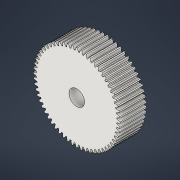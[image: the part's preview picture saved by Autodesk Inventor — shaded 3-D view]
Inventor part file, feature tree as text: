
AUTODESK INVENTOR PART (.ipt)
format: ipt  version: 2021 (Build 250183000, 183)  size: 414,720 bytes
history: native  units: mm (DEFAULTED — no unit token found)
features: plane x3, other x3, sketch x3, extrude x2
ambient origin geometry x8: Origin, YZ Plane, XZ Plane, XY Plane, X Axis, Y Axis, Z Axis, Center Point
bodies: Solid1 (feature_tree)
feature tree (11):
  extrude  "Extrusion1"  Depth=1.7mm TaperAngle=0.0deg
  plane  "Work Plane2"
  plane  "Work Plane8"
  plane  "Work Plane9"
  other  "Engrenagem reta"
  extrude  "Extrusão2"  Depth=10.0mm TaperAngle=0.0deg
  sketch  "Sketch1"  dims[d0=5.575177mm d1=1.7mm d2=0.0mm]
  sketch  "Sketch2"  dims[d3=5.4mm d4=10.0mm d5=0.0mm]
  other  "Srf1"
  sketch  "Esboço3"  dims[d16=3.597588mm d17=0.0mm d34=0.523599mm d39=0.0mm d41=0.0mm d43=3.597588mm d46=3.597588mm d47=0.0mm d48=0.0mm d49=1.0mm d50=1.7mm d51=0.0mm]
  other  "Diâmetro do flanco"
